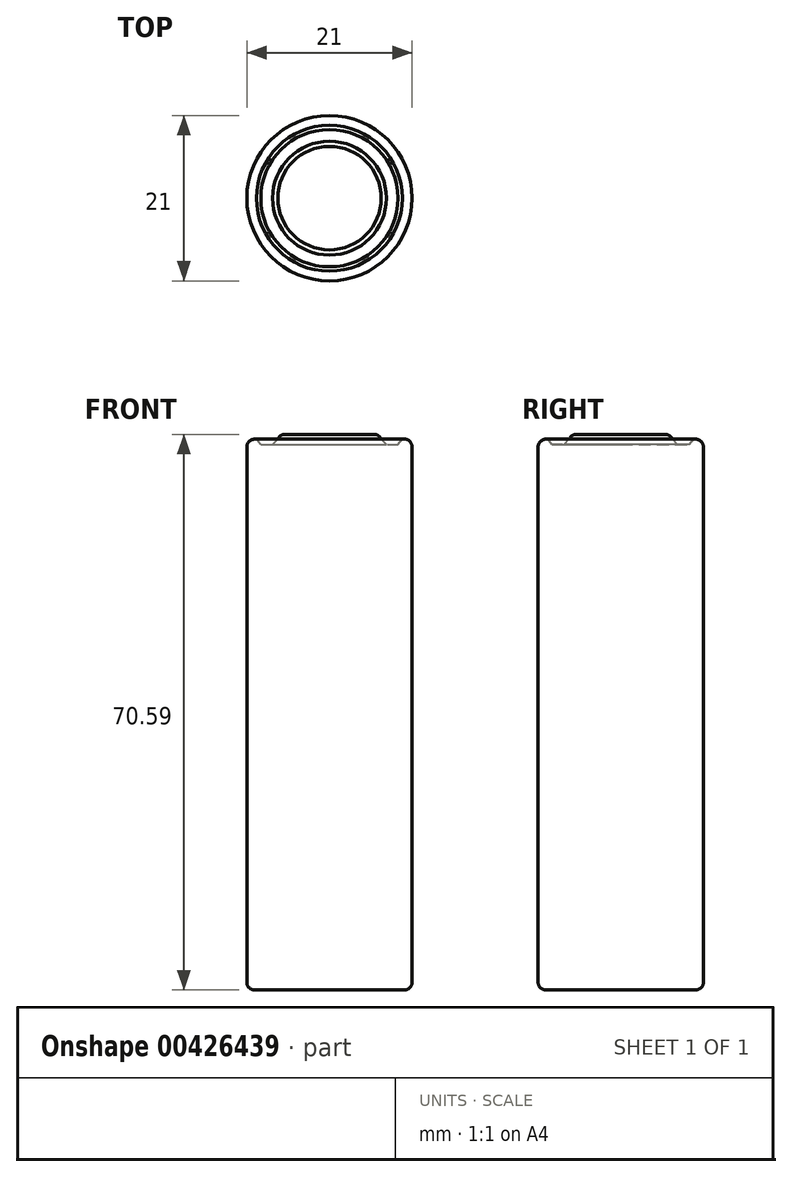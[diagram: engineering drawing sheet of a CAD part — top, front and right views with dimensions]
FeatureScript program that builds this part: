
annotation { "Feature Type Name" : "Feature", "Feature Type Description" : "" }
export const myFeature = defineFeature(function(context is Context, id is Id, definition is map)
    precondition{}
    {
        {
            var Q0;
            Q0=qCreatedBy(makeId("Front.planeOp"),FACE);
            var sketch = newSketch(context, id + "F0", { "sketchPlane" : qUnion([Q0])});
            skLineSegment(sketch, "E0.bottom", {"start": v(0, 0) * mm, "end": v(-10.5, -0.08) * mm});
            skLineSegment(sketch, "E0.left", {"start": v(0, 0) * mm, "end": v(0, 69.92) * mm});
            skLineSegment(sketch, "E0.right", {"start": v(-10.5, -0.08) * mm, "end": v(-10.5, 69.92) * mm});
            skLineSegment(sketch, "E1", {"start": v(-10.5, 69.92) * mm, "end": v(-9.27, 69.92) * mm});
            skLineSegment(sketch, "E2", {"start": v(-9.27, 69.92) * mm, "end": v(-8.72, 69.2) * mm});
            skLineSegment(sketch, "E3", {"start": v(-8.72, 69.2) * mm, "end": v(-7.23, 69.2) * mm});
            skLineSegment(sketch, "E4", {"start": v(-7.23, 69.2) * mm, "end": v(-6.56, 69.92) * mm});
            skLineSegment(sketch, "E5", {"start": v(-6.56, 69.92) * mm, "end": v(-6.24, 70.52) * mm});
            skLineSegment(sketch, "E6", {"start": v(-6.24, 70.52) * mm, "end": v(0, 70.52) * mm});
            skLineSegment(sketch, "E7", {"start": v(0, 70.52) * mm, "end": v(0, 69.92) * mm});
            skSolve(sketch);
        }
        {
            var Q0;
            Q0=makeQuery(id+"F0.imprint","IMPRINT",FACE,{"disambiguationData":[TD([[makeQuery(id+"F0.imprint","IMPRINT",EDGE,{"derivedFrom":sQuery(id+"F0.wireOp",EDGE,"E0.bottom")}),-1.0]])]});
            var Q1;
            Q1=sQuery(id+"F0.wireOp",EDGE,"E0.left");
            revolve(context, id + "F1", {"entities" : qUnion([Q0]), "axis" : qUnion([Q1]), "revolveType" : RevolveType.FULL});
        }
        {
            var Q0;
            Q0=makeQuery(id+"F1.opRevolve","SWEPT_EDGE",EDGE,{"disambiguationData":[OSD([sQuery(id+"F0.wireOp",EDGE,"E0.right"),sQuery(id+"F0.wireOp",EDGE,"6vz7Y1jI-xULs-nEBD-KH16-0xkn7j2gjJ7N")])]});
            var Q1;
            Q1=makeQuery(id+"F1.opRevolve","SWEPT_EDGE",EDGE,{"disambiguationData":[OSD([sQuery(id+"F0.wireOp",EDGE,"E0.bottom"),sQuery(id+"F0.wireOp",EDGE,"E0.right")])]});
            fillet(context, id + "F2", {"entities" : qUnion([Q0, Q1]), "radius" : 1 * mm, "tangentPropagation" : true, "allowEdgeOverflow" : false});
        }
        {
            var Q0;
            Q0=makeQuery(id+"F1.opRevolve","SWEPT_EDGE",EDGE,{"disambiguationData":[OSD([sQuery(id+"F0.wireOp",EDGE,"E5"),sQuery(id+"F0.wireOp",EDGE,"E6")])]});
            fillet(context, id + "F3", {"entities" : qUnion([Q0]), "radius" : 1 * mm, "tangentPropagation" : true, "allowEdgeOverflow" : false});
        }
    });
